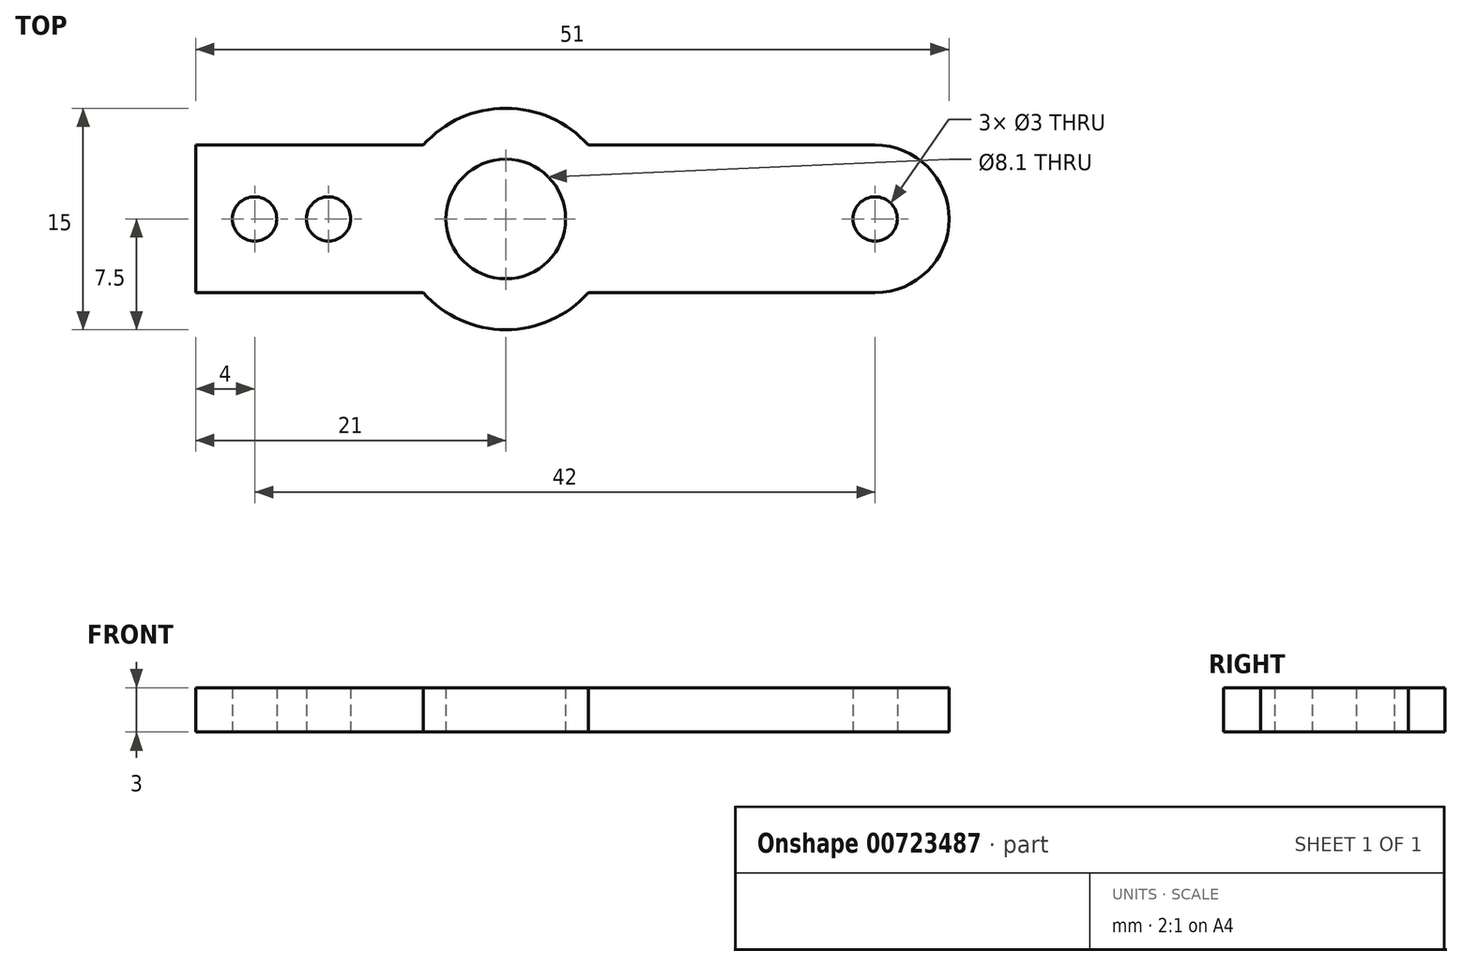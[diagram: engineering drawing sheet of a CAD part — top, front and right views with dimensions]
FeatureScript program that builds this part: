
annotation { "Feature Type Name" : "Feature", "Feature Type Description" : "" }
export const myFeature = defineFeature(function(context is Context, id is Id, definition is map)
    precondition{}
    {
        {
            var Q0;
            Q0=qCreatedBy(makeId("Top.planeOp"),FACE);
            var sketch = newSketch(context, id + "F0", { "sketchPlane" : qUnion([Q0])});
            skLineSegment(sketch, "E0.bottom", {"start": v(21, 5) * mm, "end": v(-21, 5) * mm});
            skLineSegment(sketch, "E0.top", {"start": v(21, -5) * mm, "end": v(-21, -5) * mm});
            skLineSegment(sketch, "E0.left", {"start": v(21, 5) * mm, "end": v(21, -5) * mm});
            skLineSegment(sketch, "E0.right", {"start": v(-21, 5) * mm, "end": v(-21, -5) * mm});
            skPoint(sketch, "E0.middle", {"position": v(0, 0) * mm});
            skCircle(sketch, "E1", {"center": v(-17, 0) * mm, "radius": 1.5 * mm});
            skCircle(sketch, "E2", {"center": v(-12, 0) * mm, "radius": 1.5 * mm});
            skCircle(sketch, "E3", {"center": v(0, 0) * mm, "radius": 4.05 * mm});
            skArc(sketch, "E4", {"start": v(-5.6, -5) * mm, "mid": v(0, -7.5) * mm, "end": v(5.6, -5) * mm});
            skArc(sketch, "E5.trimOffspring", {"start": v(5.6, 5) * mm, "mid": v(0, 7.5) * mm, "end": v(-5.6, 5) * mm});
            skSolve(sketch);
        }
        {
            var Q0;
            Q0 = qSketchRegion(id + "F0", true);
            extrude(context, id + "F1", {"entities" : qUnion([Q0]), "depth" : 3 * mm, "offsetDistance" : 25 * mm});
        }
        {
            var Q0;
            Q0=makeQuery(id+"F1.opExtrude","SWEPT_FACE",FACE,{"disambiguationData":[OSD([sQuery(id+"F0.wireOp",EDGE,"E0.left")])]});
            var sketch = newSketch(context, id + "F2", { "sketchPlane" : qUnion([Q0])});
            skLineSegment(sketch, "E6.bottom", {"start": v(5, 3) * mm, "end": v(-5, 3) * mm});
            skLineSegment(sketch, "E6.top", {"start": v(5, 0) * mm, "end": v(-5, 0) * mm});
            skLineSegment(sketch, "E6.left", {"start": v(5, 3) * mm, "end": v(5, 0) * mm});
            skLineSegment(sketch, "E6.right", {"start": v(-5, 3) * mm, "end": v(-5, 0) * mm});
            skSolve(sketch);
        }
        {
            var Q0;
            Q0 = qSketchRegion(id + "F2", true);
            extrude(context, id + "F3", {"entities" : qUnion([Q0]), "operationType" : NewBodyOperationType.ADD, "depth" : 9 * mm, "offsetDistance" : 25 * mm});
        }
        {
            var Q0;
            Q0=makeQuery(id+"F3.boolean.opBoolean","MERGE",FACE,{"derivedFrom":[makeQuery(id+"F1.opExtrude","CAP_FACE",FACE,{"disambiguationData":[OSD([sQuery(id+"F0.wireOp",EDGE,"E0.bottom"),sQuery(id+"F0.wireOp",EDGE,"E0.top"),sQuery(id+"F0.wireOp",EDGE,"E0.left"),sQuery(id+"F0.wireOp",EDGE,"E0.right"),sQuery(id+"F0.wireOp",EDGE,"E1"),sQuery(id+"F0.wireOp",EDGE,"E2"),sQuery(id+"F0.wireOp",EDGE,"E3")])],"isStart":true}),makeQuery(id+"F3.opExtrude","SWEPT_FACE",FACE,{"disambiguationData":[OSD([sQuery(id+"F2.wireOp",EDGE,"E6.top")])]})]});
            var sketch = newSketch(context, id + "F4", { "sketchPlane" : qUnion([Q0])});
            skCircle(sketch, "E7", {"center": v(25, 0) * mm, "radius": 1.5 * mm});
            skSolve(sketch);
        }
        {
            var Q0;
            Q0 = qSketchRegion(id + "F4", true);
            extrude(context, id + "F5", {"entities" : qUnion([Q0]), "operationType" : NewBodyOperationType.REMOVE, "oppositeDirection" : true, "depth" : 25 * mm, "offsetDistance" : 25 * mm});
        }
        {
            var Q0;
            Q0=makeQuery(id+"F3.opExtrude","CAP_EDGE",EDGE,{"disambiguationData":[OSD([sQuery(id+"F2.wireOp",EDGE,"E6.right")])],"isStart":false});
            var Q1;
            Q1=makeQuery(id+"F3.opExtrude","CAP_EDGE",EDGE,{"disambiguationData":[OSD([sQuery(id+"F2.wireOp",EDGE,"E6.left")])],"isStart":false});
            fillet(context, id + "F6", {"entities" : qUnion([Q0, Q1]), "radius" : 5 * mm, "tangentPropagation" : true, "allowEdgeOverflow" : false});
        }
    });
